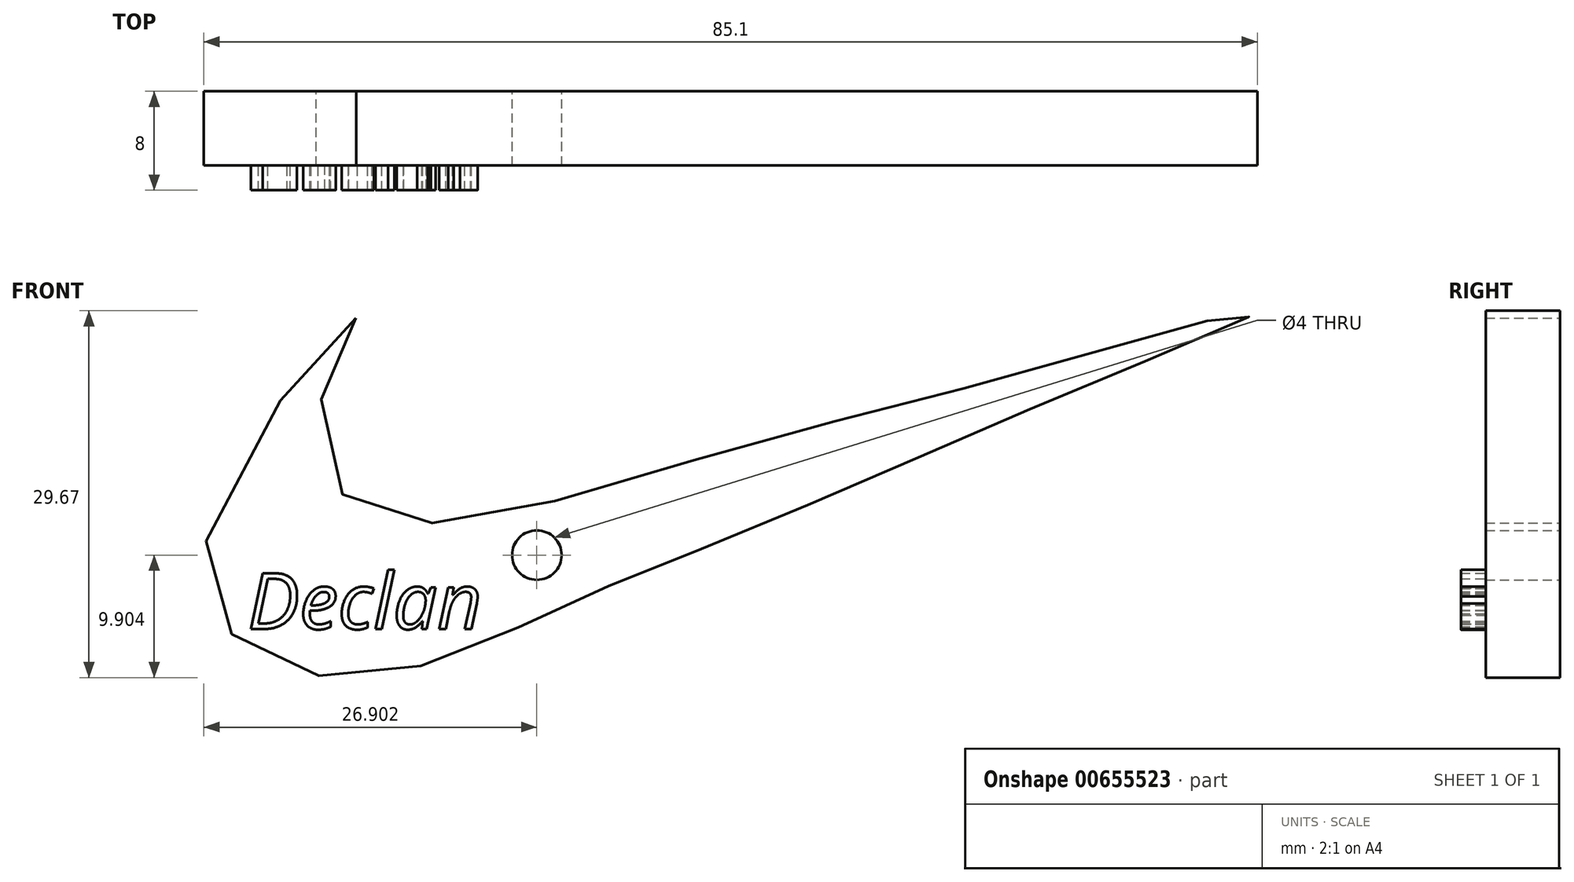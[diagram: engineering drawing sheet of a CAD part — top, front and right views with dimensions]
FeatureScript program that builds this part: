
annotation { "Feature Type Name" : "Feature", "Feature Type Description" : "" }
export const myFeature = defineFeature(function(context is Context, id is Id, definition is map)
    precondition{}
    {
        {
            var Q0;
            Q0=qCreatedBy(makeId("Front.planeOp"),FACE);
            var sketch = newSketch(context, id + "F0", { "sketchPlane" : qUnion([Q0])});
            skFitSpline(sketch, "E0", {"points": [v(-77.4, 34.96) * mm, v(-80.47, 27.28) * mm, v(-77.02, 19.6) * mm, v(-66.26, 19.02) * mm, v(-47.05, 24.4) * mm, v(-28.6, 29.2) * mm, v(-14.2, 33.23) * mm, v(-4.6, 35.54) * mm, v(-11.32, 32.47) * mm, v(-25.53, 26.5) * mm, v(-38.79, 20.75) * mm, v(-50.9, 15.75) * mm, v(-59.73, 12.1) * mm, v(-69.14, 7.88) * mm, v(-79.51, 5.96) * mm, v(-87.77, 9.8) * mm, v(-88.35, 20.55) * mm, v(-77.4, 34.96) * mm]});
            skSolve(sketch);
        }
        {
            var Q0;
            Q0 = qSketchRegion(id + "F0", true);
            extrude(context, id + "F1", {"entities" : qUnion([Q0]), "depth" : 6 * mm, "offsetDistance" : 25.4 * mm});
        }
        {
            var Q0;
            Q0=qCreatedBy(makeId("Front.planeOp"),FACE);
            var sketch = newSketch(context, id + "F2", { "sketchPlane" : qUnion([Q0])});
            skText(sketch, "E1", { "text": "Declan", "fontName": "OpenSans-Italic.ttf"});
            const initialGuessF2  = {"E1": [-0.08616, 0.00983, 1, 0, 0.00454]};
            skSetInitialGuess(sketch, initialGuessF2);
            skSolve(sketch);
        }
        {
            var Q0;
            Q0 = qSketchRegion(id + "F2", true);
            extrude(context, id + "F3", {"entities" : qUnion([Q0]), "operationType" : NewBodyOperationType.ADD, "depth" : 0.8 * mm, "offsetDistance" : 25 * mm});
        }
        {
            var Q0;
            Q0 = qSketchRegion(id + "F2", true);
            extrude(context, id + "F4", {"entities" : qUnion([Q0]), "operationType" : NewBodyOperationType.ADD, "depth" : 8 * mm, "offsetDistance" : 25 * mm});
        }
        {
            var Q0;
            Q0=qCreatedBy(makeId("Front.planeOp"),FACE);
            var sketch = newSketch(context, id + "F5", { "sketchPlane" : qUnion([Q0])});
            skPoint(sketch, "E2", {"position": v(-62.79, 15.8) * mm});
            skSolve(sketch);
        }
        {
            var Q0;
            Q0=sQuery(id+"F5.wireOp",VERTEX,"E2");
            var Q1;
            Q1=makeQuery(id+"F1.opExtrude","SWEPT_BODY",BODY,{"disambiguationData":[OSD([sQuery(id+"F0.wireOp",EDGE,"E0")])]});
            hole(context, id + "F6", {"style" : HoleStyle.SIMPLE, "endStyle" : HoleEndStyle.THROUGH, "oppositeDirection" : true, "holeDiameter" : 4 * mm, "majorDiameter" : 5 * mm, "isTappedThrough" : true, "tappedDepth" : 12 * mm, "tapClearance" : 3, "locations" : qUnion([Q0]), "scope" : qUnion([Q1])});
        }
    });
